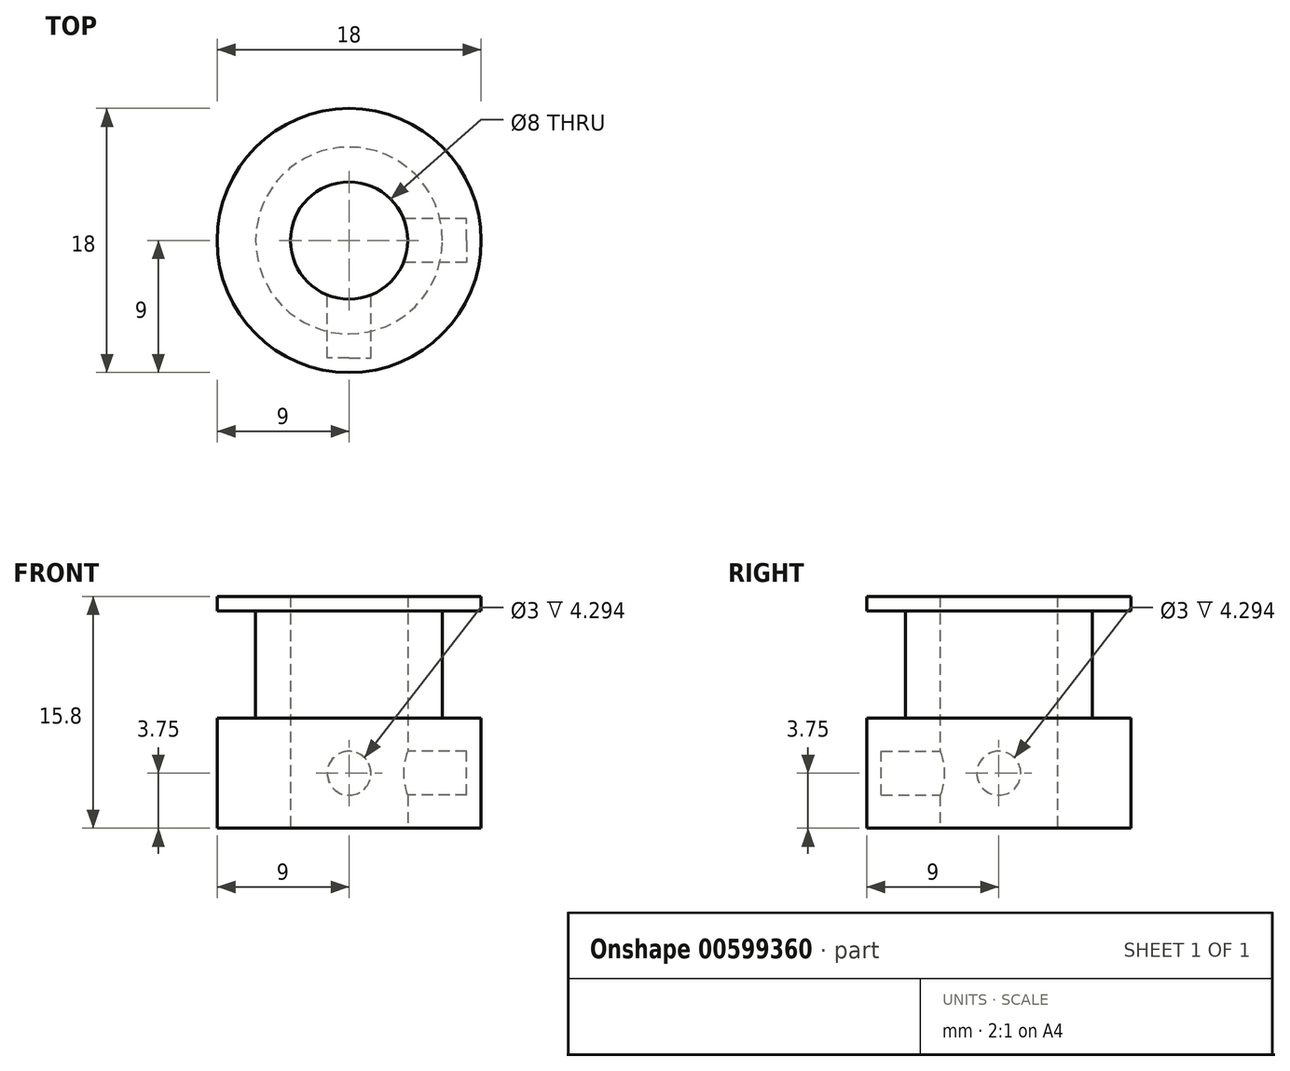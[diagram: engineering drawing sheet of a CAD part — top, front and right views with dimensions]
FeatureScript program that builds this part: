
annotation { "Feature Type Name" : "Feature", "Feature Type Description" : "" }
export const myFeature = defineFeature(function(context is Context, id is Id, definition is map)
    precondition{}
    {
        {
            var Q0;
            Q0=qCreatedBy(makeId("Top.planeOp"),FACE);
            var sketch = newSketch(context, id + "F0", { "sketchPlane" : qUnion([Q0])});
            skCircle(sketch, "E0", {"center": v(0, 0) * mm, "radius": 9 * mm});
            skCircle(sketch, "E1", {"center": v(0, 0) * mm, "radius": 4 * mm});
            skSolve(sketch);
        }
        {
            var Q0;
            Q0=qSketchRegion(id+"F0",true);
            extrude(context, id + "F1", {"entities" : qUnion([Q0]), "depth" : 7.5 * mm, "offsetDistance" : 25 * mm});
        }
        {
            var Q0;
            Q0=makeQuery(id+"F1.opExtrude","CAP_FACE",FACE,{"disambiguationData":[OSD([sQuery(id+"F0.wireOp",EDGE,"E0"),sQuery(id+"F0.wireOp",EDGE,"E1")])],"isStart":false});
            var sketch = newSketch(context, id + "F2", { "sketchPlane" : qUnion([Q0])});
            skCircle(sketch, "E2", {"center": v(0, 0) * mm, "radius": 6.37 * mm});
            skCircle(sketch, "E3.0", {"center": v(0, 0) * mm, "radius": 4 * mm});
            skSolve(sketch);
        }
        {
            var Q0;
            Q0=qSketchRegion(id+"F2",true);
            extrude(context, id + "F3", {"entities" : qUnion([Q0]), "operationType" : NewBodyOperationType.ADD, "depth" : 7.3 * mm});
        }
        {
            var Q0;
            Q0=makeQuery(id+"F3.opExtrude","CAP_FACE",FACE,{"disambiguationData":[OSD([sQuery(id+"F2.wireOp",EDGE,"E2"),sQuery(id+"F2.wireOp",EDGE,"E3.0")])],"isStart":false});
            var sketch = newSketch(context, id + "F4", { "sketchPlane" : qUnion([Q0])});
            skCircle(sketch, "E4.0", {"center": v(0, 0) * mm, "radius": 9 * mm});
            skCircle(sketch, "E4.1", {"center": v(0, 0) * mm, "radius": 4 * mm});
            skSolve(sketch);
        }
        {
            var Q0;
            Q0=qSketchRegion(id+"F4",true);
            extrude(context, id + "F5", {"entities" : qUnion([Q0]), "operationType" : NewBodyOperationType.ADD, "depth" : 1 * mm});
        }
        {
            var Q0;
            Q0=qCreatedBy(makeId("Front.planeOp"),FACE);
            var sketch = newSketch(context, id + "F6", { "sketchPlane" : qUnion([Q0])});
            skCircle(sketch, "E5", {"center": v(0, 3.75) * mm, "radius": 1.5 * mm});
            skSolve(sketch);
        }
        {
            var Q0;
            Q0=qSketchRegion(id+"F6",true);
            extrude(context, id + "F7", {"entities" : qUnion([Q0]), "operationType" : NewBodyOperationType.REMOVE, "depth" : 8 * mm});
        }
        {
            var Q0;
            Q0=qCreatedBy(makeId("Right.planeOp"),FACE);
            var sketch = newSketch(context, id + "F8", { "sketchPlane" : qUnion([Q0])});
            skCircle(sketch, "E6", {"center": v(0, 3.75) * mm, "radius": 1.5 * mm});
            skSolve(sketch);
        }
        {
            var Q0;
            Q0=qSketchRegion(id+"F8",true);
            extrude(context, id + "F9", {"entities" : qUnion([Q0]), "operationType" : NewBodyOperationType.REMOVE, "depth" : 8 * mm});
        }
    });
